FCSTD DOCUMENT  (FreeCAD 1.0R39109 (Git))
Label: NRF5340-Dongle_OUTLINE
License: All rights reserved
LicenseURL: http://en.wikipedia.org/wiki/All_rights_reserved
objects: Sketcher::SketchObject×1, PartDesign::Body×1
note: 3 computed .brp shape members not serialized (recipe doc carries the construction recipe); baked Part::Feature solids carry a one-line shape summary decoded from their .brp

FEATURE [Sketcher::SketchObject] Sketch
  ArcFitTolerance = 1e-06
  AttachmentSupport = -> [XY_Plane]
  FullyConstrained = true
  MakeInternals = false
  MapMode = 5
  sketch-geometry (52):
    g0: LineSegment StartX=-7.5 StartY=3.9 StartZ=0 EndX=-10.9 EndY=3.9 EndZ=0
    g1: LineSegment StartX=-10.9 StartY=3.9 StartZ=0 EndX=-11.4 EndY=3.585 EndZ=0
    g2: LineSegment StartX=-11.4 StartY=3.585 StartZ=0 EndX=-11.4 EndY=3.15 EndZ=0
    g3: LineSegment StartX=-11.6 StartY=2.95 StartZ=0 EndX=-11.8 EndY=2.95 EndZ=0
    g4: LineSegment StartX=-12 StartY=2.75 StartZ=0 EndX=-12 EndY=0.5 EndZ=0
    g5: LineSegment StartX=-11.8 StartY=0.3 StartZ=0 EndX=-11.6 EndY=0.3 EndZ=0
    g6: LineSegment StartX=-11.4 StartY=0.1 StartZ=0 EndX=-11.4 EndY=-0.9 EndZ=0
    g7: LineSegment StartX=-11.6 StartY=-1.1 StartZ=0 EndX=-11.8 EndY=-1.1 EndZ=0
    g8: LineSegment StartX=-12 StartY=-1.3 StartZ=0 EndX=-12 EndY=-2.75 EndZ=0
    g9: LineSegment StartX=-11.8 StartY=-2.95 StartZ=0 EndX=-11.6 EndY=-2.95 EndZ=0
    g10: LineSegment StartX=-11.4 StartY=-3.15 StartZ=0 EndX=-11.4 EndY=-3.585 EndZ=0
    g11: LineSegment [constr] StartX=-7.5 StartY=-4.3 StartZ=0 EndX=-7.5 EndY=3.9 EndZ=0
    g12: ArcOfCircle CenterX=-11.6 CenterY=0.1 CenterZ=0 NormalX=0 NormalY=0 NormalZ=1 AngleXU=0 Radius=0.2 StartAngle=0 EndAngle=1.5708
    g13: GeomPoint [constr] X=-11.4 Y=0.3 Z=0
    g14: ArcOfCircle CenterX=-11.6 CenterY=-0.9 CenterZ=0 NormalX=0 NormalY=0 NormalZ=1 AngleXU=0 Radius=0.2 StartAngle=4.71239 EndAngle=6.28319
    g15: GeomPoint [constr] X=-11.4 Y=-1.1 Z=0
    g16: ArcOfCircle CenterX=-11.8 CenterY=0.5 CenterZ=0 NormalX=0 NormalY=0 NormalZ=1 AngleXU=0 Radius=0.2 StartAngle=3.14159 EndAngle=4.71239
    g17: GeomPoint [constr] X=-12 Y=0.3 Z=0
    g18: ArcOfCircle CenterX=-11.8 CenterY=2.75 CenterZ=0 NormalX=0 NormalY=0 NormalZ=1 AngleXU=0 Radius=0.2 StartAngle=1.5708 EndAngle=3.14159
    g19: GeomPoint [constr] X=-12 Y=2.95 Z=0
    g20: ArcOfCircle CenterX=-11.6 CenterY=3.15 CenterZ=0 NormalX=0 NormalY=0 NormalZ=1 AngleXU=0 Radius=0.2 StartAngle=4.71239 EndAngle=6.28319
    g21: GeomPoint [constr] X=-11.4 Y=2.95 Z=0
    g22: ArcOfCircle CenterX=-11.8 CenterY=-1.3 CenterZ=0 NormalX=0 NormalY=0 NormalZ=1 AngleXU=0 Radius=0.2 StartAngle=1.5708 EndAngle=3.14159
    g23: GeomPoint [constr] X=-12 Y=-1.1 Z=0
    g24: ArcOfCircle CenterX=-11.8 CenterY=-2.75 CenterZ=0 NormalX=0 NormalY=0 NormalZ=1 AngleXU=0 Radius=0.2 StartAngle=3.14159 EndAngle=4.71239
    g25: GeomPoint [constr] X=-12 Y=-2.95 Z=0
    g26: ArcOfCircle CenterX=-11.6 CenterY=-3.15 CenterZ=0 NormalX=0 NormalY=0 NormalZ=1 AngleXU=0 Radius=0.2 StartAngle=0 EndAngle=1.5708
    g27: GeomPoint [constr] X=-11.4 Y=-2.95 Z=0
    g28: LineSegment StartX=-11.4 StartY=-3.585 StartZ=0 EndX=-10.9 EndY=-3.9 EndZ=0
    g29: LineSegment StartX=-10.9 StartY=-3.9 StartZ=0 EndX=-7.5 EndY=-3.9 EndZ=0
    g30: GeomPoint X=-7.5 Y=-0.2 Z=0
    g31: LineSegment [constr] StartX=-7.5 StartY=-3.9 StartZ=0 EndX=-7.5 EndY=-6 EndZ=0
    g32: LineSegment StartX=-7.5 StartY=-6 StartZ=0 EndX=11 EndY=-6 EndZ=0
    g33: LineSegment StartX=12 StartY=-5 StartZ=0 EndX=12 EndY=5 EndZ=0
    g34: LineSegment StartX=11 StartY=6 StartZ=0 EndX=-7.5 EndY=6 EndZ=0
    g35: LineSegment [constr] StartX=-7.5 StartY=6 StartZ=0 EndX=-7.5 EndY=3.9 EndZ=0
    g36: ArcOfCircle CenterX=11 CenterY=5 CenterZ=0 NormalX=0 NormalY=0 NormalZ=1 AngleXU=0 Radius=1 StartAngle=1e-16 EndAngle=1.5708
    g37: GeomPoint [constr] X=12 Y=6 Z=0
    g38: ArcOfCircle CenterX=11 CenterY=-5 CenterZ=0 NormalX=0 NormalY=0 NormalZ=1 AngleXU=0 Radius=1 StartAngle=4.71239 EndAngle=6.28319
    g39: GeomPoint [constr] X=12 Y=-6 Z=0
    g40: LineSegment StartX=-7.5 StartY=3.9 StartZ=0 EndX=-7.5 EndY=4.25 EndZ=0
    g41: LineSegment StartX=-7.5 StartY=4.25 StartZ=0 EndX=-9.5 EndY=4.25 EndZ=0
    g42: LineSegment StartX=-9.5 StartY=4.25 StartZ=0 EndX=-9.5 EndY=5 EndZ=0
    g43: LineSegment StartX=-8.5 StartY=6 StartZ=0 EndX=-7.5 EndY=6 EndZ=0
    g44: ArcOfCircle CenterX=-8.5 CenterY=5 CenterZ=0 NormalX=0 NormalY=0 NormalZ=1 AngleXU=0 Radius=1 StartAngle=1.5708 EndAngle=3.14159
    g45: GeomPoint [constr] X=-9.5 Y=6 Z=0
    g46: LineSegment StartX=-7.5 StartY=-3.9 StartZ=0 EndX=-7.5 EndY=-4.25 EndZ=0
    g47: LineSegment StartX=-7.5 StartY=-4.25 StartZ=0 EndX=-9.5 EndY=-4.25 EndZ=0
    g48: LineSegment StartX=-9.5 StartY=-4.25 StartZ=0 EndX=-9.5 EndY=-5 EndZ=0
    g49: LineSegment StartX=-8.5 StartY=-6 StartZ=0 EndX=-7.5 EndY=-6 EndZ=0
    g50: ArcOfCircle CenterX=-8.5 CenterY=-5 CenterZ=0 NormalX=0 NormalY=0 NormalZ=1 AngleXU=0 Radius=1 StartAngle=3.14159 EndAngle=4.71239
    g51: GeomPoint [constr] X=-9.5 Y=-6 Z=0
  constraints (127):
    c: Horizontal(g0)
    c: Coincident(g0,g1)
    c: Coincident(g1,g2)
    c: Vertical(g2)
    c: Horizontal(g3)
    c: Vertical(g4)
    c: Horizontal(g5)
    c: Vertical(g6)
    c: Horizontal(g7)
    c: Vertical(g8)
    c: Horizontal(g9)
    c: Coincident(g11,g0)
    c: PointOnObject(g13,g5)
    c: PointOnObject(g13,g6)
    c: Tangent(g5,g12) = 1.5708
    c: Tangent(g6,g12) = 1.5708
    c: PointOnObject(g15,g6)
    c: PointOnObject(g15,g7)
    c: Tangent(g6,g14) = 1.5708
    c: Tangent(g7,g14) = 1.5708
    c: PointOnObject(g17,g4)
    c: PointOnObject(g17,g5)
    c: Tangent(g4,g16) = -1.5708
    c: Tangent(g5,g16) = -1.5708
    c: PointOnObject(g19,g3)
    c: PointOnObject(g19,g4)
    c: Tangent(g3,g18) = -1.5708
    c: Tangent(g4,g18) = -1.5708
    c: PointOnObject(g21,g2)
    c: PointOnObject(g21,g3)
    c: Tangent(g2,g20) = 1.5708
    c: Tangent(g3,g20) = 1.5708
    c: PointOnObject(g23,g7)
    c: PointOnObject(g23,g8)
    c: Tangent(g7,g22) = -1.5708
    c: Tangent(g8,g22) = -1.5708
    c: PointOnObject(g25,g8)
    c: PointOnObject(g25,g9)
    c: Tangent(g8,g24) = -1.5708
    c: Tangent(g9,g24) = -1.5708
    c: PointOnObject(g27,g9)
    c: PointOnObject(g27,g10)
    c: Tangent(g9,g26) = 1.5708
    c: Tangent(g10,g26) = 1.5708
    c: Vertical(g10)
    c: Coincident(g10,g28)
    c: Coincident(g28,g29)
    c: Horizontal(g29)
    c: Equal(g24,g22)
    c: Equal(g22,g18)
    c: Equal(g18,g16)
    c: Radius(g24) = 0.2
    c: DistanceY(g28,g0) = 7.8
    c: DistanceX(g19,g21) = 0.6
    c: Vertical(g23,g17)
    c: Vertical(g13,g21)
    c: Vertical(g27,g15)
    c: Equal(g12,g14)
    c: Equal(g14,g22)
    c: DistanceY(g15,g13) = 1.4
    c: DistanceY(g11,g11) = 8.2
    c: Vertical(g0,g28)
    c: Equal(g1,g28)
    c: DistanceX(g25,g28) = 1.1
    c: Equal(g26,g24)
    c: Equal(g20,g18)
    c: DistanceY(g17,g19) = 2.65
    c: DistanceY(g25,g23) = 1.85
    c: DistanceY(g10,g1) = 7.17
    c: Equal(g2,g10)
    c: DistanceX(g0,g0) = 3.4
    c: Symmetric(g11,g0,g30)
    c: Vertical(g11)
    c: DistanceY(g30,g-1) = 0.2
    c: DistanceX(g19,g-1) = 12
    c: DistanceX(g29,g29) = 3.4
    c: Coincident(g29,g31)
    c: Vertical(g31)
    c: Coincident(g31,g32)
    c: Horizontal(g32)
    c: Vertical(g33)
    c: Horizontal(g34)
    c: Coincident(g34,g35)
    c: Coincident(g35,g0)
    c: Vertical(g35)
    c: PointOnObject(g37,g34)
    c: PointOnObject(g37,g33)
    c: Tangent(g34,g36) = -1.5708
    c: Tangent(g33,g36) = -1.5708
    c: PointOnObject(g39,g33)
    c: PointOnObject(g39,g32)
    c: Tangent(g33,g38) = -1.5708
    c: Tangent(g32,g38) = -1.5708
    c: Radius(g36) = 1
    c: Symmetric(g36,g38,g-1)
    c: DistanceX(g-1,g33) = 12
    c: DistanceY(g39,g37) = 12
    c: Coincident(g0,g40)
    c: PointOnObject(g40,g35)
    c: Coincident(g40,g41)
    c: Horizontal(g41)
    c: Coincident(g41,g42)
    c: Vertical(g42)
    c: Coincident(g43,g34)
    c: Horizontal(g43)
    c: PointOnObject(g45,g43)
    c: PointOnObject(g45,g42)
    c: Tangent(g43,g44) = 1.5708
    c: Tangent(g42,g44) = 1.5708
    c: Equal(g44,g36)
    c: DistanceY(g40,g40) = 0.35
    c: DistanceX(g41,g41) = 2
    c: Coincident(g29,g46)
    c: PointOnObject(g46,g31)
    c: Coincident(g46,g47)
    c: Horizontal(g47)
    c: Coincident(g47,g48)
    c: Vertical(g48)
    c: Coincident(g49,g31)
    c: Horizontal(g49)
    c: Equal(g46,g40)
    c: PointOnObject(g51,g48)
    c: PointOnObject(g51,g49)
    c: Tangent(g48,g50) = -1.5708
    c: Tangent(g49,g50) = -1.5708
    c: Equal(g50,g44)
    c: Vertical(g47,g41)
FEATURE [PartDesign::Body] Body
  AllowCompound = false
  Group = -> [Sketch]
  Origin = -> Origin
